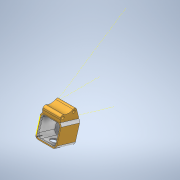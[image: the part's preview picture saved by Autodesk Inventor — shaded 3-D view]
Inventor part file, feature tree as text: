
AUTODESK INVENTOR PART (.ipt)
format: ipt  version: 2020 (Build 240168000, 168)  size: 244,736 bytes
history: native  units: mm
features: other x3, sketch x3, extrude x1, projected_geometry x1
ambient origin geometry x8: Origin, YZ Plane, XZ Plane, XY Plane, X Axis, Y Axis, Z Axis, Center Point
bodies: Solid2 (feature_tree)
feature tree (8):
  other  "V2 modular session template.iam"
  other  "V2 modular session camera case.ipt:1"
  other  "V2 modular session frame mount.ipt:1"
  extrude  "Extrusion1"  Depth=10.0mm TaperAngle=0.0deg
  sketch  "Sketch6"  dims[d1=10.0mm d2=10.0mm d3=0.0mm]
  sketch  "Sketch7"
  sketch  "Sketch8"
  projected_geometry  "Projected Loop1"
